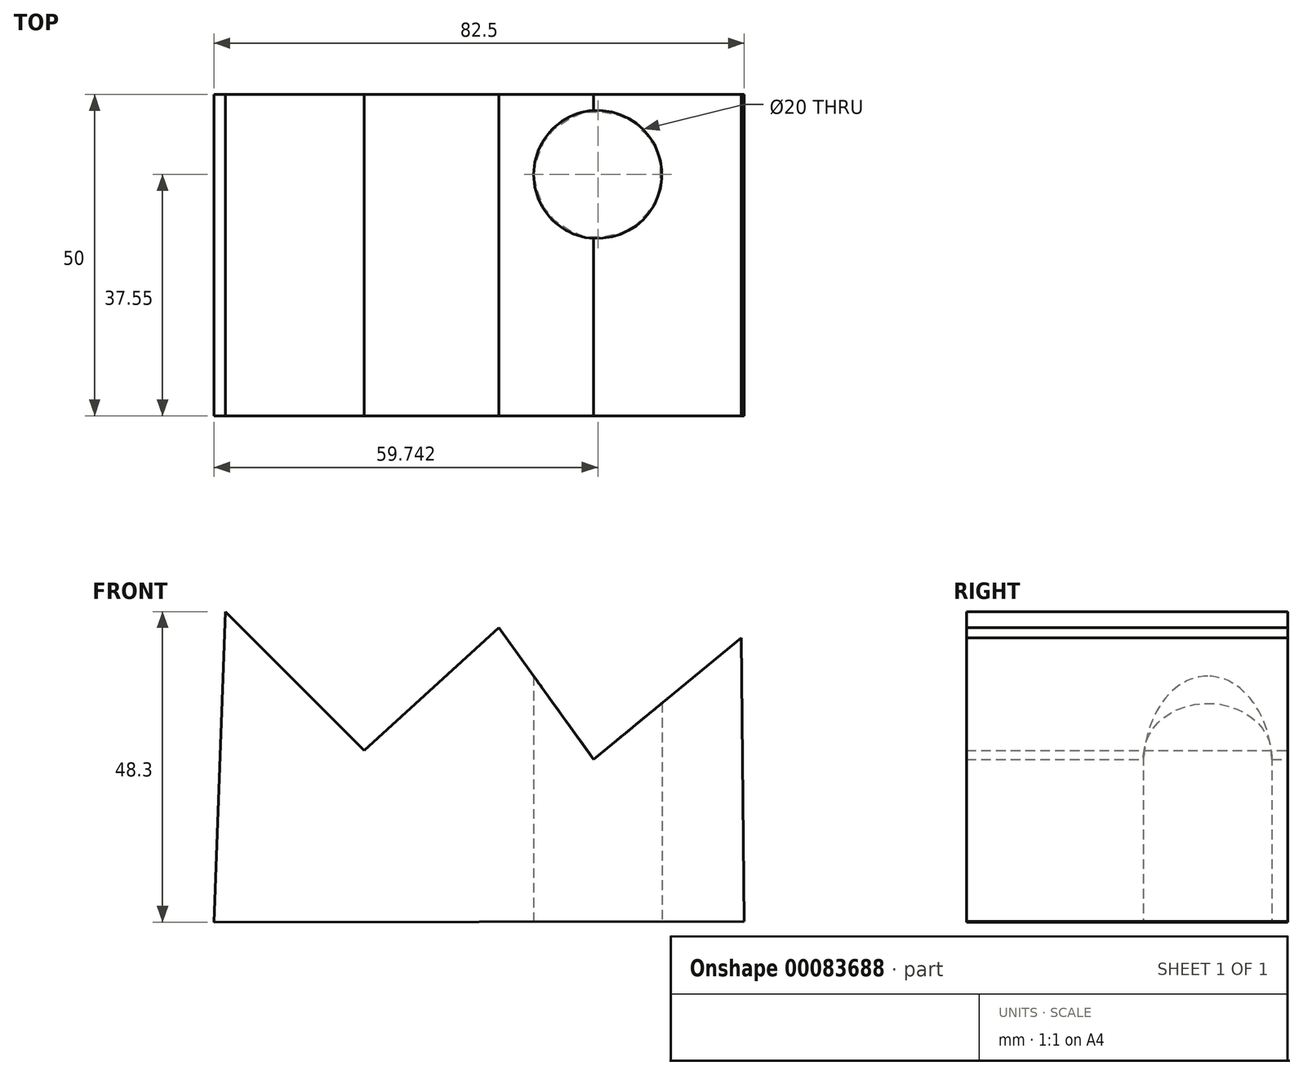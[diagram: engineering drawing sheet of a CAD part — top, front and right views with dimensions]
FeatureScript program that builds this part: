
annotation { "Feature Type Name" : "Feature", "Feature Type Description" : "" }
export const myFeature = defineFeature(function(context is Context, id is Id, definition is map)
    precondition{}
    {
        {
            var Q0;
            Q0=qCreatedBy(makeId("Front.planeOp"),FACE);
            var sketch = newSketch(context, id + "F0", { "sketchPlane" : qUnion([Q0])});
            skLineSegment(sketch, "E0", {"start": v(-44.1, 0) * mm, "end": v(-42.27, 48.3) * mm});
            skLineSegment(sketch, "E1", {"start": v(-42.27, 48.3) * mm, "end": v(-20.68, 26.7) * mm});
            skLineSegment(sketch, "E2", {"start": v(-20.68, 26.7) * mm, "end": v(0.23, 45.8) * mm});
            skLineSegment(sketch, "E3", {"start": v(0.23, 45.8) * mm, "end": v(15, 25.34) * mm});
            skLineSegment(sketch, "E4", {"start": v(15, 25.34) * mm, "end": v(37.95, 44.2) * mm});
            skLineSegment(sketch, "E5", {"start": v(37.95, 44.2) * mm, "end": v(38.4, 0.11) * mm});
            skLineSegment(sketch, "E6", {"start": v(38.4, 0.11) * mm, "end": v(-44.1, 0) * mm});
            skSolve(sketch);
        }
        {
            var Q0;
            Q0=makeQuery(id+"F0.imprint","IMPRINT",FACE,{"disambiguationData":[TD([[makeQuery(id+"F0.imprint","IMPRINT",EDGE,{"derivedFrom":sQuery(id+"F0.wireOp",EDGE,"E0")}),-1.0]])]});
            extrude(context, id + "F1", {"entities" : qUnion([Q0]), "depth" : 25 * mm});
        }
        {
            var Q0;
            Q0=qCreatedBy(makeId("Top.planeOp"),FACE);
            var sketch = newSketch(context, id + "F2", { "sketchPlane" : qUnion([Q0])});
            skCircle(sketch, "E7", {"center": v(15.65, -12.45) * mm, "radius": 10 * mm});
            skSolve(sketch);
        }
        {
            var Q0;
            Q0 = qSketchRegion(id + "F2", true);
            var Q1;
            Q1=sQuery(id+"F2.wireOp",EDGE,"E7");
            extrude(context, id + "F3", {"entities" : qUnion([Q0]), "operationType" : NewBodyOperationType.REMOVE, "surfaceEntities" : qUnion([Q1]), "endBound" : BoundingType.THROUGH_ALL, "depth" : 40 * mm});
        }
        {
            var Q0;
            Q0=makeQuery(id+"F1.opExtrude","CAP_FACE",FACE,{"disambiguationData":[OSD([sQuery(id+"F0.wireOp",EDGE,"E0"),sQuery(id+"F0.wireOp",EDGE,"E1"),sQuery(id+"F0.wireOp",EDGE,"E2"),sQuery(id+"F0.wireOp",EDGE,"E3"),sQuery(id+"F0.wireOp",EDGE,"E4"),sQuery(id+"F0.wireOp",EDGE,"E5"),sQuery(id+"F0.wireOp",EDGE,"E6")])],"isStart":false});
            extrude(context, id + "F4", {"entities" : qUnion([Q0]), "operationType" : NewBodyOperationType.ADD, "depth" : 25 * mm});
        }
    });
